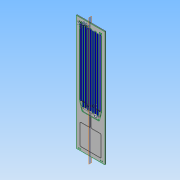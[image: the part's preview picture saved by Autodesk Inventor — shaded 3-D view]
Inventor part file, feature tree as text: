
AUTODESK INVENTOR PART (.ipt)
format: ipt  version: 2013 (Build 170138000, 138)  size: 423,424 bytes
history: native  units: in
note: dims shown in document units (in); Inventor stores cm internally (conversion verified against a paired STEP export)
features: other x15, extrude x4, hole x1, plane x1
ambient origin geometry x8: Origin, YZ Plane, XZ Plane, XY Plane, X Axis, Y Axis, Z Axis, Center Point
bodies: Solid1 (feature_tree)
feature tree (21):
  other  "Blocks"
  extrude  "Stock Extrusion"  Depth=23.8125in
  extrude  "Main rope pocket"  Depth=96.0in
  other  "Side profile reference"
  hole  "Hole1"  [1 undecoded]
  plane  "Work Plane1"
  extrude  "Through Panel Extrusion5"  Depth=58.0in
  other  "Exclaim Point"
  other  "Removal extra wood"
  other  "SignCenter"
  extrude  "Extrusion7"  Depth=1.0in
  other  "Stock"
  other  "LEDPocket"
  other  "TwoLineColumn"
  other  "TwoLineColumnEnd"
  other  "15mm Neon profile"
  other  "U Bolt hole and bore"
  other  "U-Bolt holes"
  other  "WeatherProof panel"
  other  "15mm Neon profile:1"
  other  "15mm Neon profile:2"
note: 1 required parameter value undecoded (feature->parameter linkage not recoverable at this tier; creation-order binding heuristic only, values carry confidence <= 0.55)
